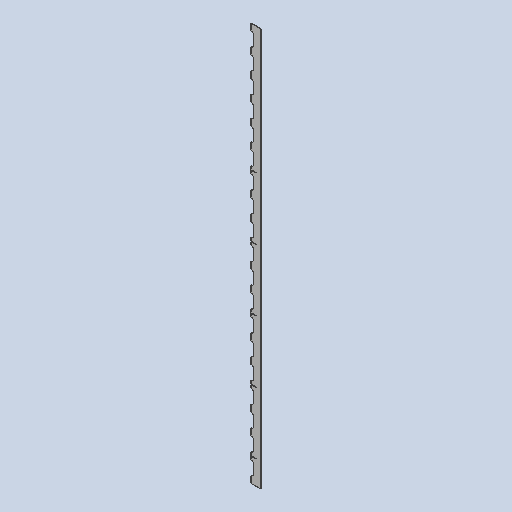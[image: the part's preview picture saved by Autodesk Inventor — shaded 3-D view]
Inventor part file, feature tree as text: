
AUTODESK INVENTOR PART (.ipt)
format: ipt  version: 2025 (Build 290162010, 162A)  size: 287,232 bytes
history: native  units: mm
features: sketch x3, extrude x2, pattern_linear x2, other x2, sheet_metal_op x1, projected_geometry x1
ambient origin geometry x8: Origin, YZ Plane, XZ Plane, XY Plane, X Axis, Y Axis, Z Axis, Center Point
bodies: Body1 (feature_tree)
feature tree (11):
  sheet_metal_op  "Face2"
  extrude  "Extrusion2"  Depth=2897.0mm
  pattern_linear  "Rectangular Pattern2"  Count1=2  [1 undecoded]
  extrude  "Extrusion4"  Depth=450.0mm
  pattern_linear  "Rectangular Pattern3"  Count1=19  [1 undecoded]
  sketch  "Sketch6"  dims[d26=70.28909mm d27=2897.0mm]
  other  "Plate4"
  sketch  "Sketch7"  dims[d28=3.0mm]
  projected_geometry  "Projected Loop1"
  sketch  "Sketch8"  dims[d32=0.0mm d33=0.0mm d37=20.0mm d38=100.0mm d39=190.0mm d41=150.0mm d57=3.2mm d58=36.289mm d59=173.0mm d60=0.0mm d61=0.0mm d62=50.0mm d64=450.0mm]
  other  "Definition1"
note: 2 required parameter values undecoded (feature->parameter linkage not recoverable at this tier; creation-order binding heuristic only, values carry confidence <= 0.55)
